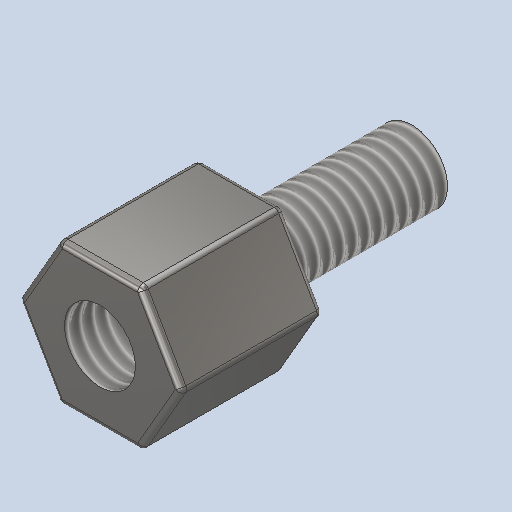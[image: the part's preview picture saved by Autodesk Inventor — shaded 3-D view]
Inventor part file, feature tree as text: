
AUTODESK INVENTOR PART (.ipt)
format: ipt  version: 2023 (Build 270158000, 158)  size: 192,000 bytes
history: native  units: mm
features: extrude x3, sketch x3, thread x2, fillet x1
ambient origin geometry x8: Origin, YZ Plane, XZ Plane, XY Plane, X Axis, Y Axis, Z Axis, Center Point
bodies: Solid1 (feature_tree)
feature tree (9):
  extrude  "Extrusion1"  Depth=5.0mm
  extrude  "Extrusion2"  Depth=2.5mm
  extrude  "Extrusion3"  TaperAngle=0.0deg  [1 undecoded]
  thread  "Thread1"  [1 undecoded]
  thread  "Thread2"  [1 undecoded]
  fillet  "Fillet1"  [1 undecoded]
  sketch  "Sketch1"  dims[d0=5.0mm d1=5.0mm]
  sketch  "Sketch2"  dims[d2=0.0mm d3=2.5mm]
  sketch  "Sketch3"  dims[d4=3.0mm d5=0.0mm d6=2.5mm d7=6.0mm d8=0.0mm d9=10.0mm d10=0.0mm d11=10.0mm d12=0.0mm d13=0.2mm d14=0.2mm]
note: 4 required parameter values undecoded (feature->parameter linkage not recoverable at this tier; creation-order binding heuristic only, values carry confidence <= 0.55)
